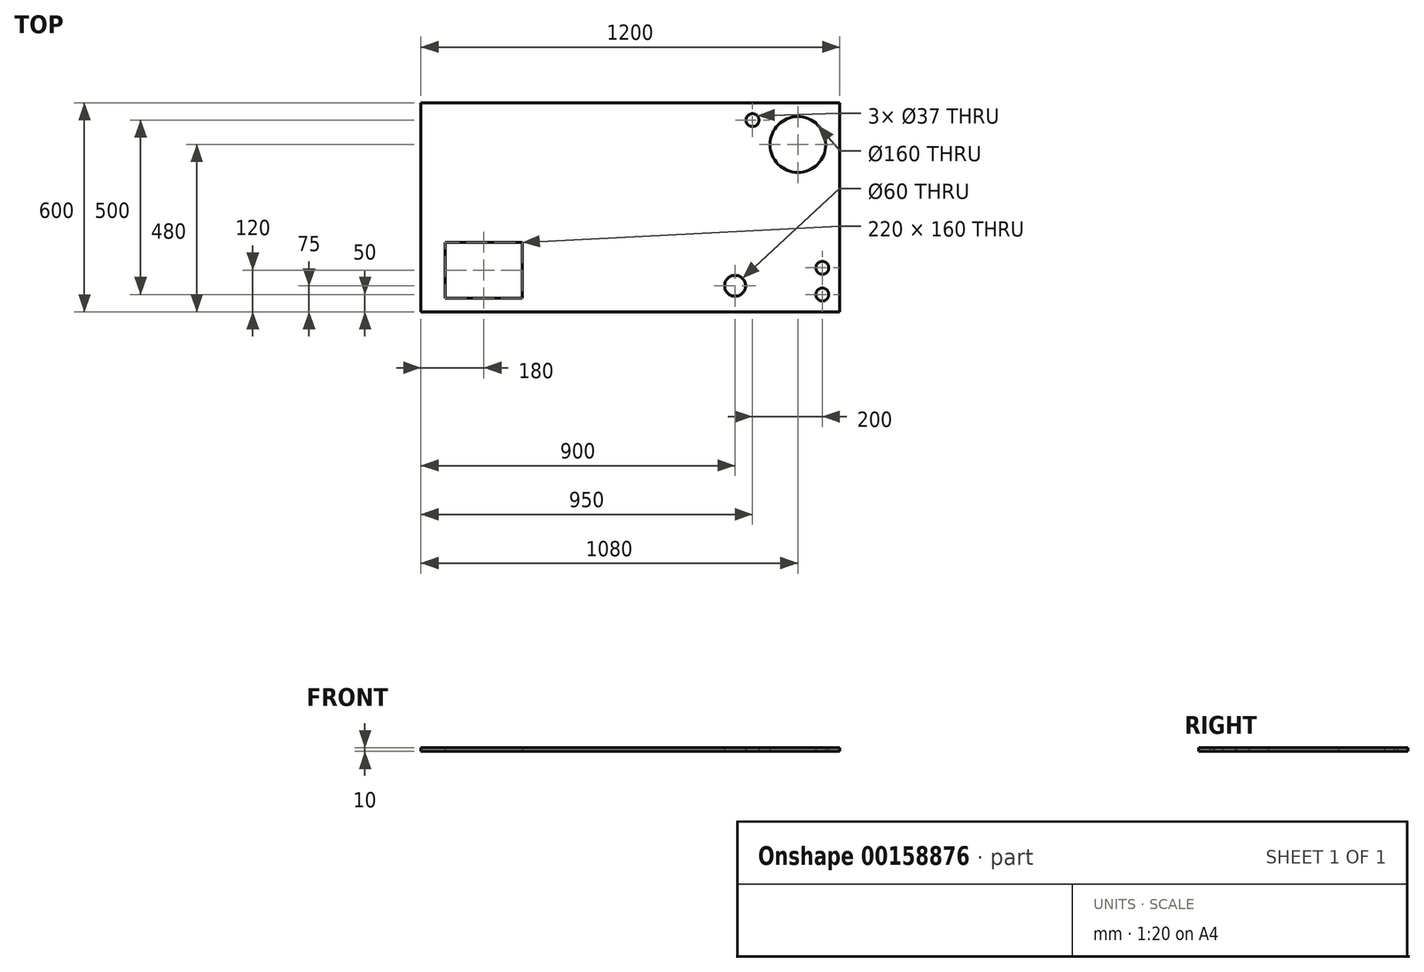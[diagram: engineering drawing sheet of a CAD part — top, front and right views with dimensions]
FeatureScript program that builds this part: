
annotation { "Feature Type Name" : "Feature", "Feature Type Description" : "" }
export const myFeature = defineFeature(function(context is Context, id is Id, definition is map)
    precondition{}
    {
        {
            var Q0;
            Q0=qCreatedBy(makeId("Top.planeOp"),FACE);
            var sketch = newSketch(context, id + "F0", { "sketchPlane" : qUnion([Q0])});
            skLineSegment(sketch, "E0.bottom", {"start": v(-600, -300) * mm, "end": v(600, -300) * mm});
            skLineSegment(sketch, "E0.top", {"start": v(-600, 300) * mm, "end": v(600, 300) * mm});
            skLineSegment(sketch, "E0.left", {"start": v(-600, -300) * mm, "end": v(-600, 300) * mm});
            skLineSegment(sketch, "E0.right", {"start": v(600, -300) * mm, "end": v(600, 300) * mm});
            skPoint(sketch, "E0.middle", {"position": v(0, 0) * mm});
            skCircle(sketch, "E1", {"center": v(480, 180) * mm, "radius": 80 * mm});
            skCircle(sketch, "E2", {"center": v(350, 250) * mm, "radius": 18.5 * mm});
            skCircle(sketch, "E3", {"center": v(550, -250) * mm, "radius": 18.5 * mm});
            skCircle(sketch, "E4", {"center": v(550, -173.5) * mm, "radius": 18.5 * mm});
            skCircle(sketch, "E5", {"center": v(300, -225) * mm, "radius": 30 * mm});
            skLineSegment(sketch, "E6.bottom", {"start": v(-310, -260) * mm, "end": v(-530, -260) * mm});
            skLineSegment(sketch, "E6.top", {"start": v(-310, -100) * mm, "end": v(-530, -100) * mm});
            skLineSegment(sketch, "E6.left", {"start": v(-310, -260) * mm, "end": v(-310, -100) * mm});
            skLineSegment(sketch, "E6.right", {"start": v(-530, -260) * mm, "end": v(-530, -100) * mm});
            skPoint(sketch, "E6.middle", {"position": v(-420, -180) * mm});
            skSolve(sketch);
        }
        {
            var Q0;
            Q0 = qSketchRegion(id + "F0", true);
            extrude(context, id + "F1", {"entities" : qUnion([Q0]), "depth" : 10 * mm});
        }
    });
